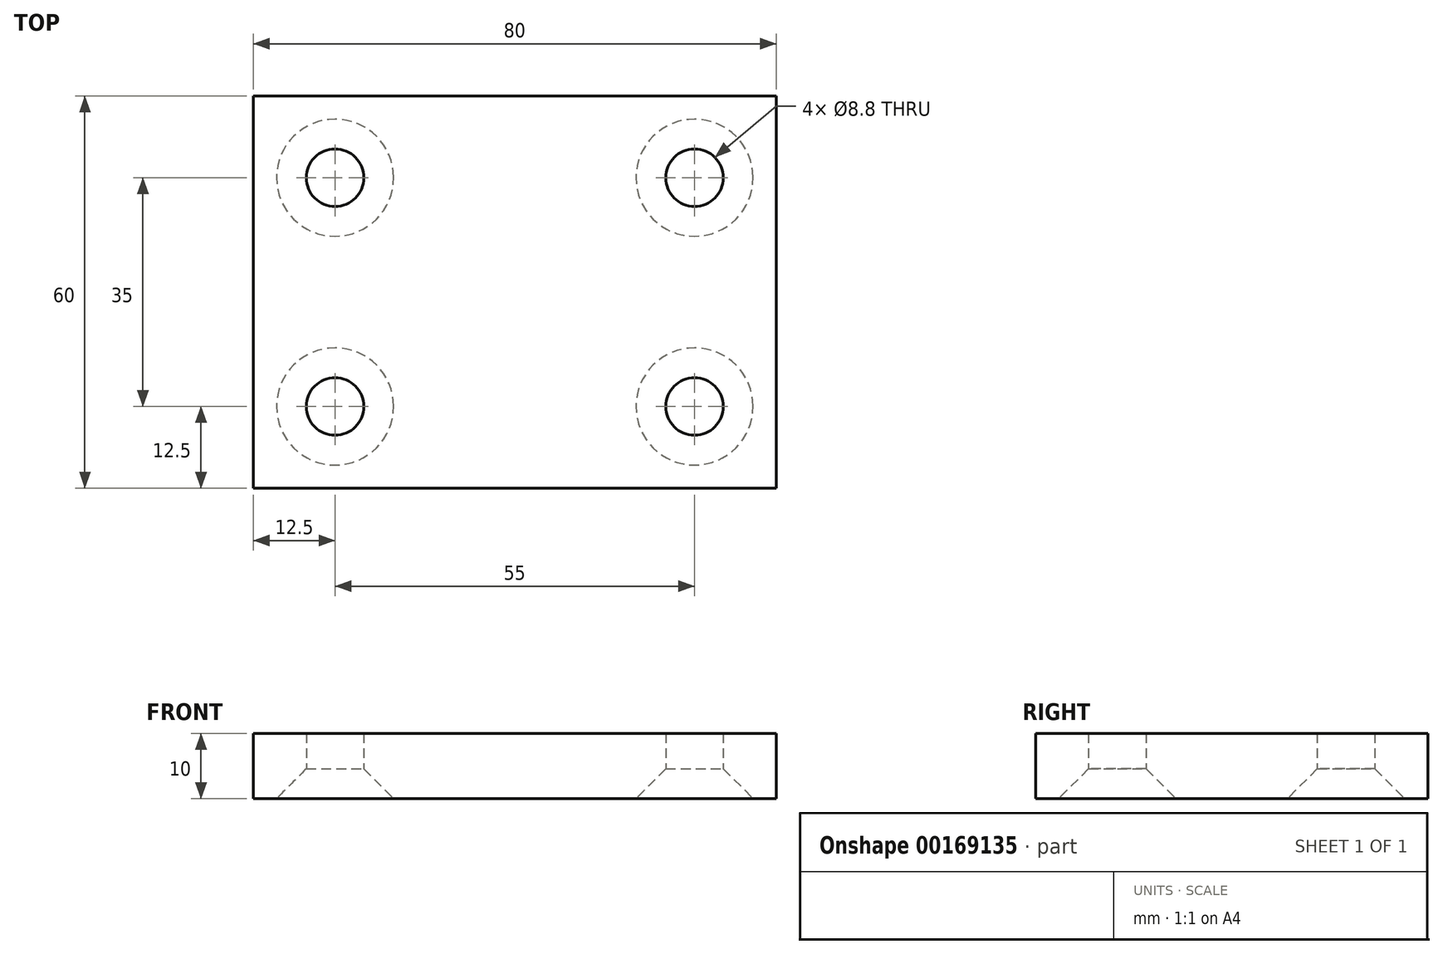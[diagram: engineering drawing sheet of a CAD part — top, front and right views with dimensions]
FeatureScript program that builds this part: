
annotation { "Feature Type Name" : "Feature", "Feature Type Description" : "" }
export const myFeature = defineFeature(function(context is Context, id is Id, definition is map)
    precondition{}
    {
        {
            var Q0;
            Q0=qCreatedBy(makeId("Top.planeOp"),FACE);
            var sketch = newSketch(context, id + "F0", { "sketchPlane" : qUnion([Q0])});
            skLineSegment(sketch, "E0.bottom", {"start": v(0, 0) * mm, "end": v(80, 0) * mm});
            skLineSegment(sketch, "E0.top", {"start": v(0, 60) * mm, "end": v(80, 60) * mm});
            skLineSegment(sketch, "E0.left", {"start": v(0, 0) * mm, "end": v(0, 60) * mm});
            skLineSegment(sketch, "E0.right", {"start": v(80, 0) * mm, "end": v(80, 60) * mm});
            skLineSegment(sketch, "E1.0", {"start": v(12.5, 47.5) * mm, "end": v(67.5, 47.5) * mm});
            skLineSegment(sketch, "E1.1", {"start": v(12.5, 12.5) * mm, "end": v(12.5, 47.5) * mm});
            skLineSegment(sketch, "E1.2", {"start": v(12.5, 12.5) * mm, "end": v(67.5, 12.5) * mm});
            skLineSegment(sketch, "E1.3", {"start": v(67.5, 12.5) * mm, "end": v(67.5, 47.5) * mm});
            skSolve(sketch);
        }
        {
            var Q0;
            Q0=makeQuery(id+"F0.imprint","IMPRINT",FACE,{"disambiguationData":[TD([[makeQuery(id+"F0.imprint","IMPRINT",EDGE,{"derivedFrom":sQuery(id+"F0.wireOp",EDGE,"E1.0")}),-1.0]])]});
            var Q1;
            Q1=makeQuery(id+"F0.imprint","IMPRINT",FACE,{"disambiguationData":[TD([[makeQuery(id+"F0.imprint","IMPRINT",EDGE,{"derivedFrom":sQuery(id+"F0.wireOp",EDGE,"E0.bottom")}),1.0]])]});
            extrude(context, id + "F1", {"entities" : qUnion([Q0, Q1]), "depth" : 10 * mm});
        }
        {
            var Q0;
            Q0=sQuery(id+"F0.wireOp",VERTEX,"E1.2.start");
            var Q1;
            Q1=sQuery(id+"F0.wireOp",VERTEX,"E1.3.start");
            var Q2;
            Q2=sQuery(id+"F0.wireOp",VERTEX,"E1.3.end");
            var Q3;
            Q3=sQuery(id+"F0.wireOp",VERTEX,"E1.1.end");
            var Q4;
            Q4=makeQuery(id+"F1.opExtrude","SWEPT_BODY",BODY,{"disambiguationData":[OSD([sQuery(id+"F0.wireOp",EDGE,"E0.bottom"),sQuery(id+"F0.wireOp",EDGE,"E0.top"),sQuery(id+"F0.wireOp",EDGE,"E0.left"),sQuery(id+"F0.wireOp",EDGE,"E0.right")])]});
            hole(context, id + "F2", {"style" : HoleStyle.C_SINK, "endStyle" : HoleEndStyle.THROUGH, "oppositeDirection" : true, "standardTappedOrClearance" : lookupTablePath({ "standard" : "ISO", "fit" : "Normal", "size" : "M8", "type" : "Clearance" }), "standardBlindInLast" : lookupTablePath({ "fit" : "Standard", "standard" : "ISO", "size" : "M8", "type" : "Clearance" }), "holeDiameter" : 8.8 * mm, "cSinkDiameter" : 17.92 * mm, "cSinkAngle" : 90 * degree, "locations" : qUnion([Q0, Q1, Q2, Q3]), "scope" : qUnion([Q4]), "isTappedThrough" : true});
        }
    });
